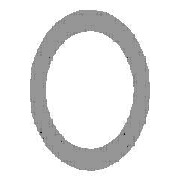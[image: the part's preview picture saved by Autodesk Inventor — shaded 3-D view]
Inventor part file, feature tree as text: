
AUTODESK INVENTOR PART (.ipt)
format: ipt  version: 2013 (Build 170138000, 138)  size: 161,792 bytes
history: native  units: mm (DEFAULTED — no unit token found)
features: other x5, sketch x2, sweep x1, plane x1
ambient origin geometry x8: Origin, YZ Plane, XZ Plane, XY Plane, X Axis, Y Axis, Z Axis, Center Point
bodies: Solid1 (feature_tree), Body (feature_tree)
feature tree (9):
  parser-record x1  (decoder bookkeeping rows leaked as tree rows — omitted from the tree; the rows remain in map.json)
  other  "Driven Length"
  other  "Start plane"
  other  "End plane"
  sweep  "Sweep Path"
  other  "Orientation Work Plane"
  sketch  "Sketch3"  dims[d0=33.401mm d1=3.3782mm]
  plane  "Work Plane3"
  sketch  "Sketch4"  dims[d4=-0.0mm d5=106.029537mm d6=90.0deg d7=106.029537mm d8=0.0mm]
